# Revit family: Faucet-Lavatory-KOHLER-Devonshire-K-394-4
name_source: partatom
category: Plumbing Fixtures
revit_build: Autodesk Revit 2015 (Build: 20140606_1530(x64)
units: mm (PartAtom-declared; Revit-internal decimal feet)

## types (6) — shared parameters
ADA Compliant = Yes
Assembly Code = D2010900
CW Connection = Yes
Date Modified = 09/22/2017
Default Elevation = 36"
Description = Devonshire Widespread bathroom sink faucet
Faucet Hole Spacing = 8"
Flow Rate = 1 GPM
HW Connection = Yes
Height = 4 21/32"
Inlet Connector = Inlet Connection
Length = 7 13/16"
Manufacturer = Kohler
MasterFormat 1995 = 15410
MasterFormat 2004 = 22.41.39
Material = Solid Brass Construction
Outlet Connector = Outlet Connection
Pressure = 60.00 psi
Product Documentation Link = http://www.us.kohler.com
Product Name = Devonshire
Product Page URL = http://www.us.kohler.com
Spout Reach = 6"
URL = http://www.us.kohler.com
Waste Connection = Yes
Width = 14"

## per-type parameters (varying)
| type | Finish | Model | Type |
| CP-Polished Chrome | Kohler-Metal-CP-Polished_Chrome | K-394-4-CP | 1 |
| SN-Vibrant Polished Nickel | Kohler-Metal-SN-Vibrant_Polished_Nickel | K-394-4-SN | 2 |
| PB-Vibrant Polished Brass | Kohler-Metal-PB-Vibrant_Polished_Brass | K-394-4-PB | 3 |
| BN-Vibrant Brushed Nickel | Kohler-Metal-BN-Vibrant_Brushed_Nickel | K-394-4-BN | 4 |
| BV-Vibrant Brushed Bronze | Kohler-Metal-BV-Brushed_Bronze | K-394-4-BV | 5 |
| 2BZ-Oil Rubbed Bronze | Kohler-Metal-2BZ-Oil_Rubbed_Bronze | K-394-4-2BZ | 6 |

## geometry (parser evidence)
native form markers: Sweep x8
no freeform markers — native parametric forms only
